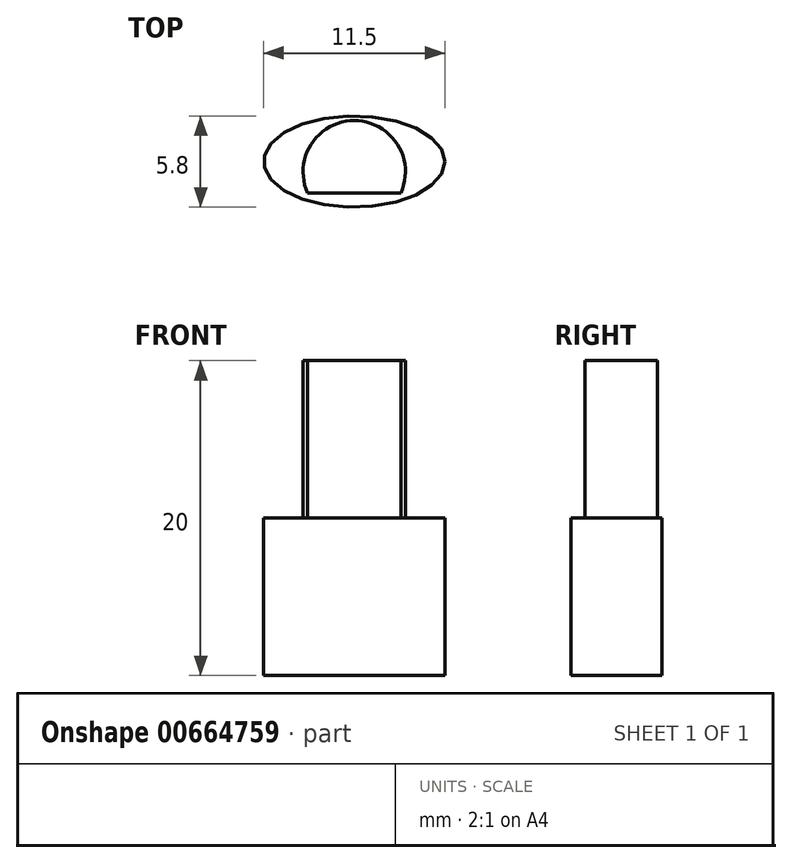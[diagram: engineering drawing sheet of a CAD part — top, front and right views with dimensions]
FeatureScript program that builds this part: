
annotation { "Feature Type Name" : "Feature", "Feature Type Description" : "" }
export const myFeature = defineFeature(function(context is Context, id is Id, definition is map)
    precondition{}
    {
        {
            var Q0;
            Q0=qCreatedBy(makeId("Top.planeOp"),FACE);
            var sketch = newSketch(context, id + "F0", { "sketchPlane" : qUnion([Q0])});
            skEllipse(sketch, "E0", {"center": v(0, 0) * mm, "majorRadius": 5.75 * mm, "minorRadius": 2.9 * mm, "majorAxis": v(1, 0)});
            skSolve(sketch);
        }
        {
            var Q0;
            Q0=makeQuery(id+"F0.imprint","IMPRINT",FACE,{"disambiguationData":[TD([[makeQuery(id+"F0.imprint","IMPRINT",EDGE,{"derivedFrom":sQuery(id+"F0.wireOp",EDGE,"E0")}),1.0]])]});
            extrude(context, id + "F1", {"entities" : qUnion([Q0]), "depth" : 10 * mm, "offsetDistance" : 25 * mm});
        }
        {
            var Q0;
            Q0=makeQuery(id+"F1.opExtrude","CAP_FACE",FACE,{"disambiguationData":[OSD([sQuery(id+"F0.wireOp",EDGE,"E0")])],"isStart":false});
            var sketch = newSketch(context, id + "F2", { "sketchPlane" : qUnion([Q0])});
            skLineSegment(sketch, "E1", {"start": v(0, 0) * mm, "end": v(0, 2.6) * mm});
            skLineSegment(sketch, "E2", {"start": v(0, 2.6) * mm, "end": v(0, -0.65) * mm});
            skArc(sketch, "E3", {"start": v(2.96, -2) * mm, "mid": v(0, 2.6) * mm, "end": v(-2.96, -2) * mm});
            skLineSegment(sketch, "E4", {"start": v(0, 0) * mm, "end": v(0, -2) * mm});
            skLineSegment(sketch, "E5", {"start": v(0, -2) * mm, "end": v(2.96, -2) * mm});
            skLineSegment(sketch, "E6", {"start": v(0, -2) * mm, "end": v(-2.96, -2) * mm});
            skSolve(sketch);
        }
        {
            var Q0;
            Q0 = qSketchRegion(id + "F2", true);
            extrude(context, id + "F3", {"entities" : qUnion([Q0]), "operationType" : NewBodyOperationType.ADD, "depth" : 10 * mm, "offsetDistance" : 25 * mm});
        }
    });
